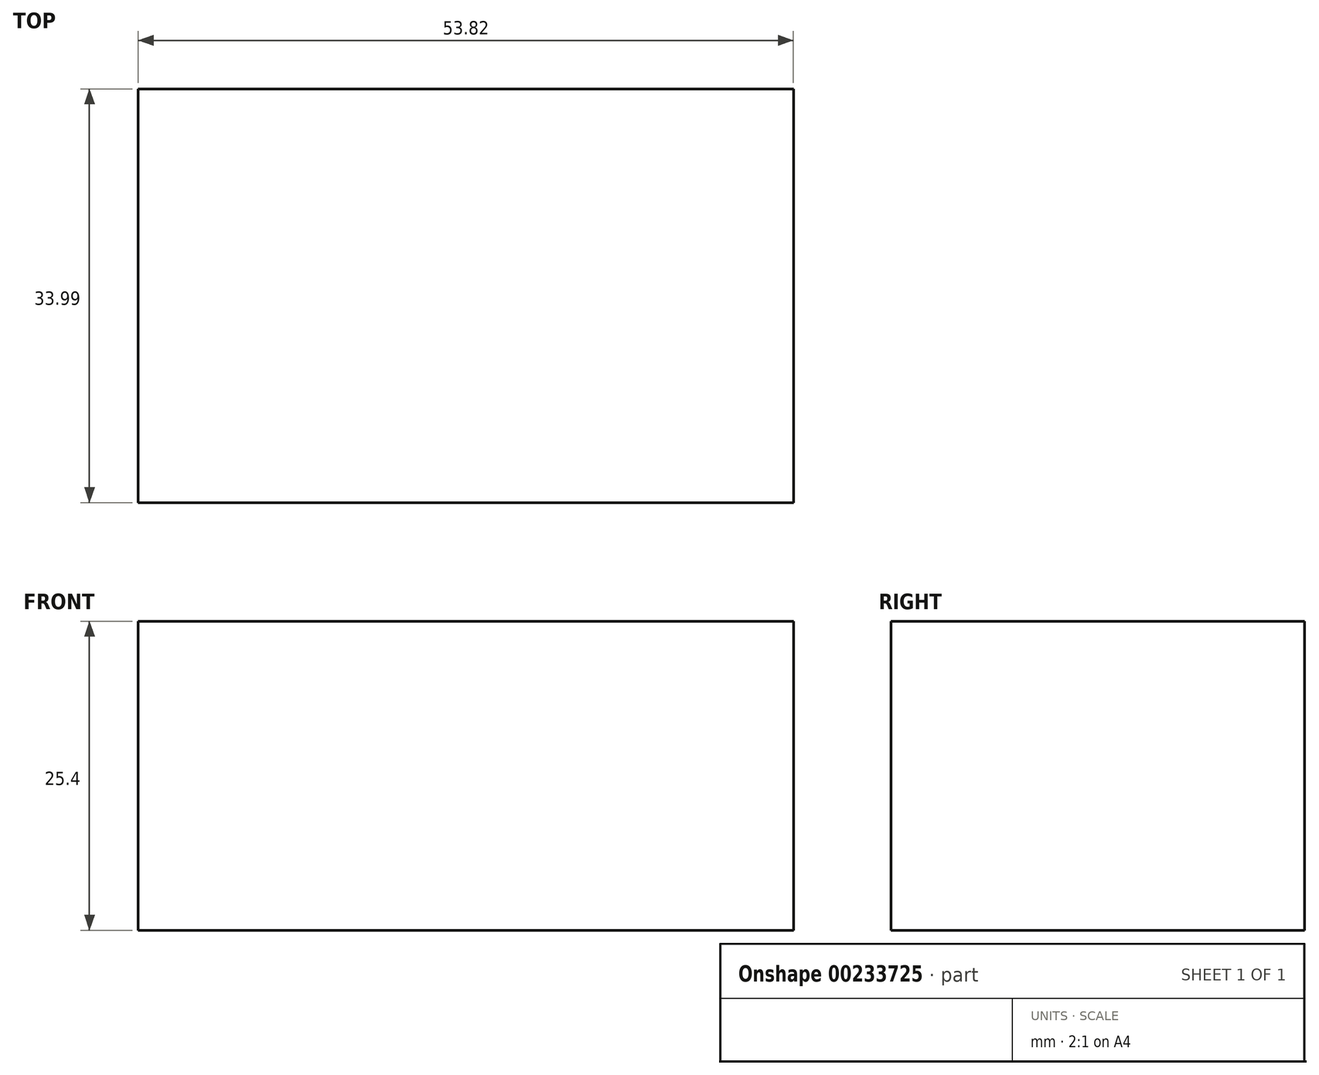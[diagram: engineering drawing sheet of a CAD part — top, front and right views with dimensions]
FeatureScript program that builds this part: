
annotation { "Feature Type Name" : "Feature", "Feature Type Description" : "" }
export const myFeature = defineFeature(function(context is Context, id is Id, definition is map)
    precondition{}
    {
        {
            var Q0;
            Q0=qCreatedBy(makeId("Top.planeOp"),FACE);
            var sketch = newSketch(context, id + "F0", { "sketchPlane" : qUnion([Q0])});
            skLineSegment(sketch, "E0.bottom", {"start": v(0, 0) * mm, "end": v(53.82, 0) * mm});
            skLineSegment(sketch, "E0.top", {"start": v(0, 33.99) * mm, "end": v(53.82, 33.99) * mm});
            skLineSegment(sketch, "E0.left", {"start": v(0, 0) * mm, "end": v(0, 33.99) * mm});
            skLineSegment(sketch, "E0.right", {"start": v(53.82, 0) * mm, "end": v(53.82, 33.99) * mm});
            skLineSegment(sketch, "E1.0", {"start": v(-6.35, 40.34) * mm, "end": v(60.17, 40.34) * mm});
            skLineSegment(sketch, "E1.1", {"start": v(-6.35, -6.35) * mm, "end": v(-6.35, 40.34) * mm});
            skLineSegment(sketch, "E1.2", {"start": v(-6.35, -6.35) * mm, "end": v(60.17, -6.35) * mm});
            skLineSegment(sketch, "E1.3", {"start": v(60.17, -6.35) * mm, "end": v(60.17, 40.34) * mm});
            skSolve(sketch);
        }
        {
            var Q0;
            Q0=makeQuery(id+"F0.imprint","IMPRINT",FACE,{"disambiguationData":[TD([[makeQuery(id+"F0.imprint","IMPRINT",EDGE,{"derivedFrom":sQuery(id+"F0.wireOp",EDGE,"E0.bottom")}),1.0]])]});
            extrude(context, id + "F1", {"entities" : qUnion([Q0]), "depth" : 25.4 * mm});
        }
    });
